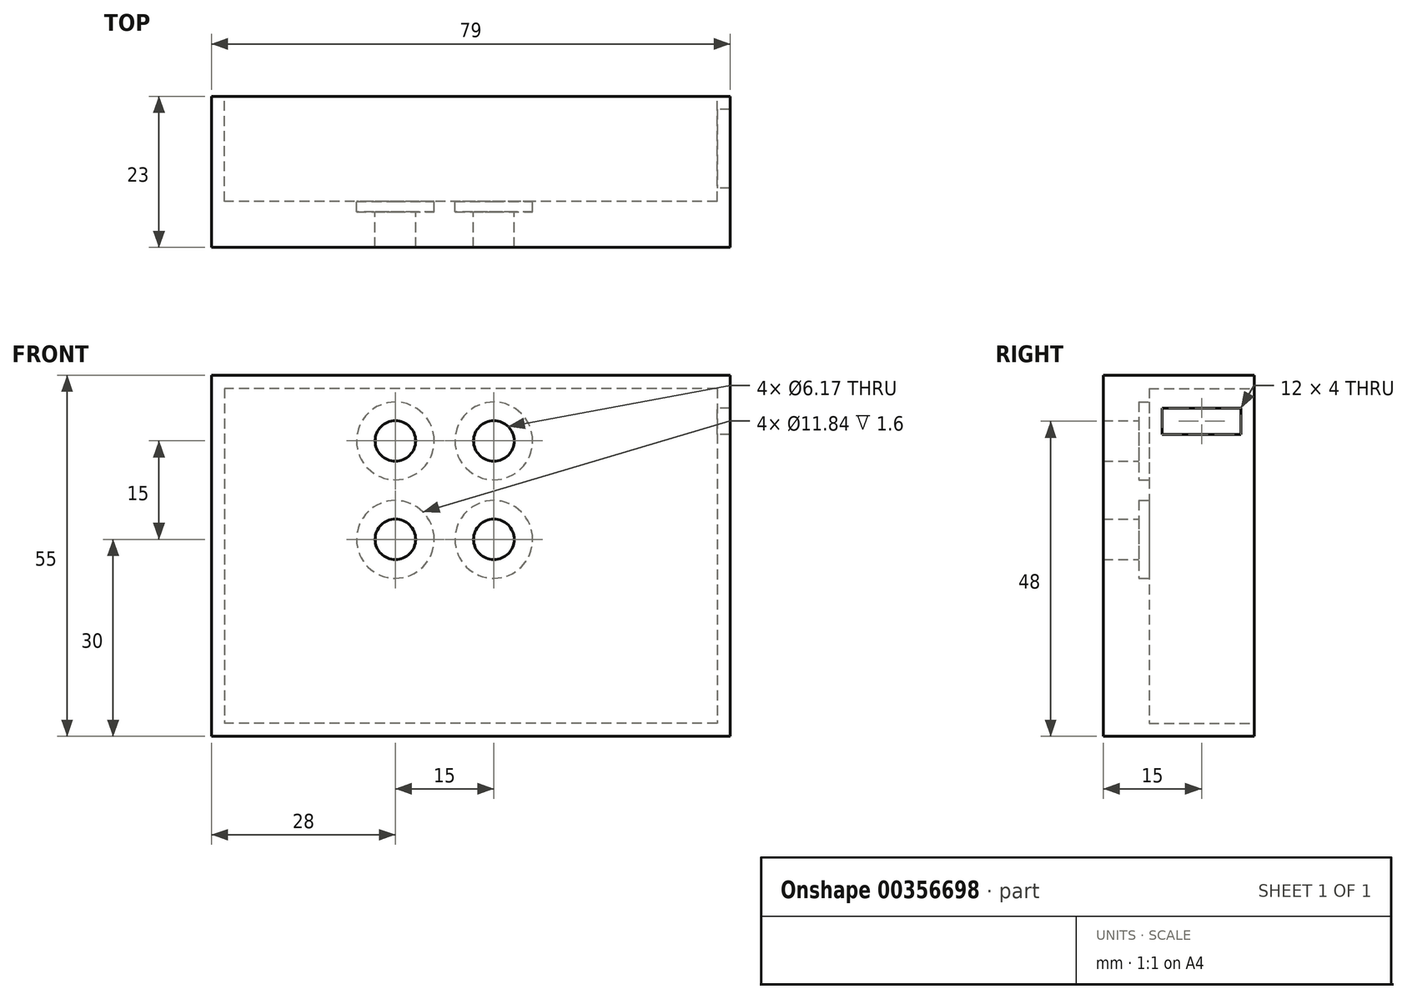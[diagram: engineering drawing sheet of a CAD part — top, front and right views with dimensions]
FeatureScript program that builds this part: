
annotation { "Feature Type Name" : "Feature", "Feature Type Description" : "" }
export const myFeature = defineFeature(function(context is Context, id is Id, definition is map)
    precondition{}
    {
        {
            var Q0;
            Q0=qCreatedBy(makeId("Front.planeOp"),FACE);
            var sketch = newSketch(context, id + "F0", { "sketchPlane" : qUnion([Q0])});
            skLineSegment(sketch, "E0.bottom", {"start": v(39.5, -27.5) * mm, "end": v(-39.5, -27.5) * mm});
            skLineSegment(sketch, "E0.top", {"start": v(39.5, 27.5) * mm, "end": v(-39.5, 27.5) * mm});
            skLineSegment(sketch, "E0.left", {"start": v(39.5, -27.5) * mm, "end": v(39.5, 27.5) * mm});
            skLineSegment(sketch, "E0.right", {"start": v(-39.5, -27.5) * mm, "end": v(-39.5, 27.5) * mm});
            skPoint(sketch, "E0.middle", {"position": v(0, 0) * mm});
            skSolve(sketch);
        }
        {
            var Q0;
            Q0=qSketchRegion(id+"F0",true);
            extrude(context, id + "F1", {"entities" : qUnion([Q0]), "depth" : 23 * mm});
        }
        {
            var Q0;
            Q0=makeQuery(id+"F1.opExtrude","CAP_FACE",FACE,{"disambiguationData":[OSD([sQuery(id+"F0.wireOp",EDGE,"E0.bottom"),sQuery(id+"F0.wireOp",EDGE,"E0.top"),sQuery(id+"F0.wireOp",EDGE,"E0.left"),sQuery(id+"F0.wireOp",EDGE,"E0.right")])],"isStart":true});
            var sketch = newSketch(context, id + "F2", { "sketchPlane" : qUnion([Q0])});
            skLineSegment(sketch, "E1.0", {"start": v(-39.5, 27.5) * mm, "end": v(39.5, 27.5) * mm, "construction": true});
            skLineSegment(sketch, "E1.1", {"start": v(-39.5, -27.5) * mm, "end": v(-39.5, 27.5) * mm, "construction": true});
            skLineSegment(sketch, "E1.2", {"start": v(-39.5, -27.5) * mm, "end": v(39.5, -27.5) * mm, "construction": true});
            skLineSegment(sketch, "E1.3", {"start": v(39.5, -27.5) * mm, "end": v(39.5, 27.5) * mm, "construction": true});
            skLineSegment(sketch, "E2.bottom", {"start": v(-37.5, 25.5) * mm, "end": v(37.5, 25.5) * mm});
            skLineSegment(sketch, "E2.top", {"start": v(-37.5, -25.5) * mm, "end": v(37.5, -25.5) * mm});
            skLineSegment(sketch, "E2.left", {"start": v(-37.5, 25.5) * mm, "end": v(-37.5, -25.5) * mm});
            skLineSegment(sketch, "E2.right", {"start": v(37.5, 25.5) * mm, "end": v(37.5, -25.5) * mm});
            skSolve(sketch);
        }
        {
            var Q0;
            Q0=qSketchRegion(id+"F2",true);
            extrude(context, id + "F3", {"entities" : qUnion([Q0]), "operationType" : NewBodyOperationType.REMOVE, "oppositeDirection" : true, "depth" : (21 - 5) * mm});
        }
        {
            var Q0;
            Q0=qCreatedBy(makeId("Right.planeOp"),FACE);
            var sketch = newSketch(context, id + "F4", { "sketchPlane" : qUnion([Q0])});
            skLineSegment(sketch, "E3.bottom", {"start": v(-14, 22.5) * mm, "end": v(-2, 22.5) * mm});
            skLineSegment(sketch, "E3.top", {"start": v(-14, 18.5) * mm, "end": v(-2, 18.5) * mm});
            skLineSegment(sketch, "E3.left", {"start": v(-14, 22.5) * mm, "end": v(-14, 18.5) * mm});
            skLineSegment(sketch, "E3.right", {"start": v(-2, 22.5) * mm, "end": v(-2, 18.5) * mm});
            skLineSegment(sketch, "E4.0.0", {"start": v(-16, 25.5) * mm, "end": v(-16, -25.5) * mm, "construction": true});
            skLineSegment(sketch, "E4.0.2", {"start": v(-16, -25.5) * mm, "end": v(-16, 25.5) * mm, "construction": true});
            skSolve(sketch);
        }
        {
            var Q0;
            Q0=qSketchRegion(id+"F4",true);
            extrude(context, id + "F5", {"entities" : qUnion([Q0]), "operationType" : NewBodyOperationType.REMOVE, "depth" : 55 * mm});
        }
        {
            var Q0;
            Q0=qCreatedBy(makeId("Front.planeOp"),FACE);
            var sketch = newSketch(context, id + "F6", { "sketchPlane" : qUnion([Q0])});
            skCircle(sketch, "E5", {"center": v(-11.5, 17.5) * mm, "radius": 3.09 * mm});
            skCircle(sketch, "E6", {"center": v(-11.5, 2.5) * mm, "radius": 3.09 * mm});
            skCircle(sketch, "E7", {"center": v(3.5, 2.5) * mm, "radius": 3.09 * mm});
            skCircle(sketch, "E8", {"center": v(3.5, 17.5) * mm, "radius": 3.09 * mm});
            skSolve(sketch);
        }
        {
            var Q0;
            Q0=qSketchRegion(id+"F6",true);
            extrude(context, id + "F7", {"entities" : qUnion([Q0]), "operationType" : NewBodyOperationType.REMOVE, "depth" : 25 * mm});
        }
        {
            var Q0;
            Q0=makeQuery(id+"F3.boolean.opBoolean","COPY",FACE,{"derivedFrom":makeQuery(id+"F3.opExtrude","CAP_FACE",FACE,{"disambiguationData":[OSD([sQuery(id+"F2.wireOp",EDGE,"E2.bottom"),sQuery(id+"F2.wireOp",EDGE,"E2.top"),sQuery(id+"F2.wireOp",EDGE,"E2.left"),sQuery(id+"F2.wireOp",EDGE,"E2.right")])],"isStart":false})});
            var sketch = newSketch(context, id + "F8", { "sketchPlane" : qUnion([Q0])});
            skCircle(sketch, "E9", {"center": v(-3.5, 17.5) * mm, "radius": 5.92 * mm});
            skCircle(sketch, "E10", {"center": v(-3.5, 2.5) * mm, "radius": 5.92 * mm});
            skCircle(sketch, "E11", {"center": v(11.5, 2.5) * mm, "radius": 5.92 * mm});
            skCircle(sketch, "E12", {"center": v(11.5, 17.5) * mm, "radius": 5.92 * mm});
            skSolve(sketch);
        }
        {
            var Q0;
            Q0=qSketchRegion(id+"F8",true);
            extrude(context, id + "F9", {"entities" : qUnion([Q0]), "operationType" : NewBodyOperationType.REMOVE, "oppositeDirection" : true, "depth" : 1.6 * mm});
        }
    });
